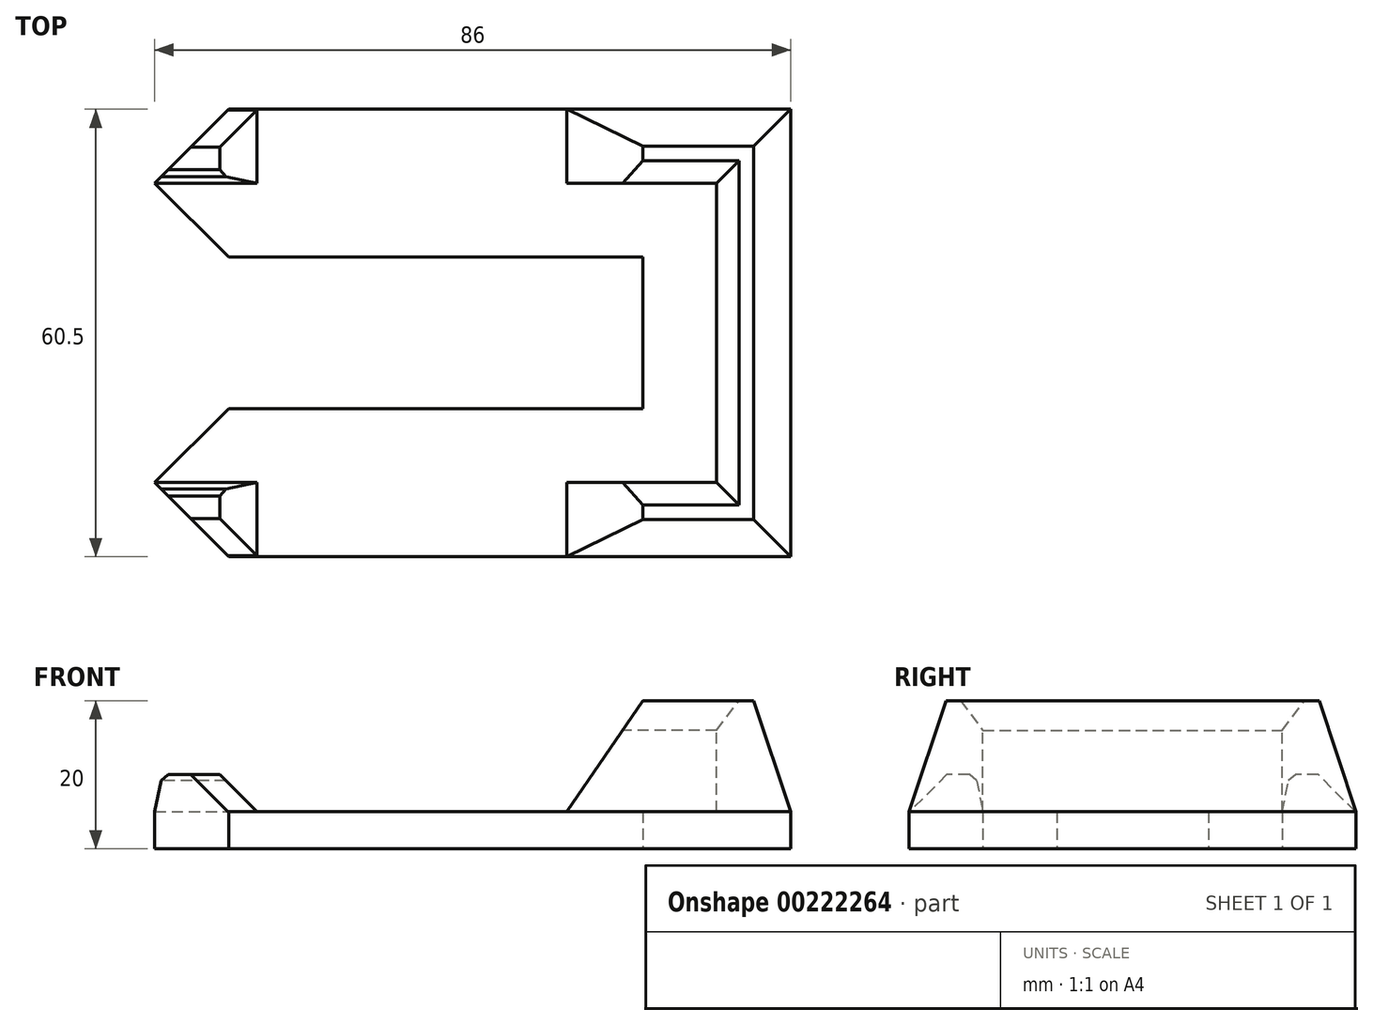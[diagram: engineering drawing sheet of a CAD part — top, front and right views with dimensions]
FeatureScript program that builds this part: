
annotation { "Feature Type Name" : "Feature", "Feature Type Description" : "" }
export const myFeature = defineFeature(function(context is Context, id is Id, definition is map)
    precondition{}
    {
        {
            var Q0;
            Q0=qCreatedBy(makeId("Top.planeOp"),FACE);
            var sketch = newSketch(context, id + "F0", { "sketchPlane" : qUnion([Q0])});
            skLineSegment(sketch, "E0.bottom", {"start": v(76, -20.25) * mm, "end": v(-76, -20.25) * mm, "construction": true});
            skLineSegment(sketch, "E0.top", {"start": v(76, 20.25) * mm, "end": v(-76, 20.25) * mm, "construction": true});
            skLineSegment(sketch, "E0.left", {"start": v(76, -20.25) * mm, "end": v(76, 20.25) * mm, "construction": true});
            skLineSegment(sketch, "E0.right", {"start": v(-76, -20.25) * mm, "end": v(-76, 20.25) * mm, "construction": true});
            skPoint(sketch, "E0.middle", {"position": v(0, 0) * mm});
            skLineSegment(sketch, "E1.bottom", {"start": v(86, -30.25) * mm, "end": v(-86, -30.25) * mm});
            skLineSegment(sketch, "E1.top", {"start": v(86, 30.25) * mm, "end": v(-86, 30.25) * mm});
            skLineSegment(sketch, "E1.left", {"start": v(86, -30.25) * mm, "end": v(86, 30.25) * mm});
            skLineSegment(sketch, "E1.right", {"start": v(-86, -30.25) * mm, "end": v(-86, 30.25) * mm});
            skSolve(sketch);
        }
        {
            var Q0;
            Q0=qCreatedBy(makeId("Top.planeOp"),FACE);
            cPlane(context, id + "F1", {"entities" : qUnion([Q0]), "cplaneType" : CPlaneType.OFFSET, "offset" : 15 * mm, "width" : 150 * mm, "height" : 150 * mm});
        }
        {
            var Q0;
            Q0=qCreatedBy(id+"F1.planeOp",FACE);
            var sketch = newSketch(context, id + "F2", { "sketchPlane" : qUnion([Q0])});
            skPoint(sketch, "E2.0", {"position": v(-86, -30.25) * mm});
            skPoint(sketch, "E3.0", {"position": v(-76, -20.25) * mm});
            skLineSegment(sketch, "E4", {"start": v(-76, 0) * mm, "end": v(-76, -20.25) * mm});
            skLineSegment(sketch, "E5", {"start": v(-76, -20.25) * mm, "end": v(-86, -30.25) * mm, "construction": true});
            skPoint(sketch, "E6", {"position": v(-81, -25.25) * mm});
            skLineSegment(sketch, "E7", {"start": v(-76, 0) * mm, "end": v(-81, 0) * mm});
            skLineSegment(sketch, "E8", {"start": v(-81, 0) * mm, "end": v(-81, -25.25) * mm});
            skLineSegment(sketch, "E9", {"start": v(-76, -20.25) * mm, "end": v(-66, -20.25) * mm});
            skLineSegment(sketch, "E10", {"start": v(-66, -20.25) * mm, "end": v(-66, -25.25) * mm});
            skLineSegment(sketch, "E11", {"start": v(-66, -25.25) * mm, "end": v(-81, -25.25) * mm});
            skSolve(sketch);
        }
        {
            var Q0;
            Q0=qCreatedBy(makeId("Top.planeOp"),FACE);
            var sketch = newSketch(context, id + "F3", { "sketchPlane" : qUnion([Q0])});
            skPoint(sketch, "E12.0", {"position": v(-86, -30.25) * mm});
            skPoint(sketch, "E13.0", {"position": v(-76, -20.25) * mm});
            skLineSegment(sketch, "E14", {"start": v(-86, -30.25) * mm, "end": v(-86, 0) * mm});
            skLineSegment(sketch, "E15", {"start": v(-86, 0) * mm, "end": v(-76, 0) * mm});
            skLineSegment(sketch, "E16", {"start": v(-76, 0) * mm, "end": v(-76, -20.25) * mm});
            skLineSegment(sketch, "E17", {"start": v(-76, -20.25) * mm, "end": v(-86, -30.25) * mm, "construction": true});
            skLineSegment(sketch, "E18.MirrorCS", {"start": v(-55.75, -20.25) * mm, "end": v(-76, -20.25) * mm});
            skLineSegment(sketch, "E19.MirrorCS", {"start": v(-86, -30.25) * mm, "end": v(-55.75, -30.25) * mm});
            skLineSegment(sketch, "E20.MirrorCS", {"start": v(-55.75, -30.25) * mm, "end": v(-55.75, -20.25) * mm});
            skLineSegment(sketch, "E21", {"start": v(0, 0) * mm, "end": v(-88.2, 0) * mm, "construction": true});
            skSolve(sketch);
        }
        {
            var Q0;
            Q0=makeQuery(id+"F0.imprint","IMPRINT",FACE,{"disambiguationData":[TD([[makeQuery(id+"F0.imprint","IMPRINT",EDGE,{"derivedFrom":sQuery(id+"F0.wireOp",EDGE,"E1.bottom")}),-1.0]])]});
            extrude(context, id + "F4", {"entities" : qUnion([Q0]), "oppositeDirection" : true, "depth" : 5 * mm});
        }
        {
            var Q1;
            Q1=makeQuery(id+"F3.imprint","IMPRINT",FACE,{"disambiguationData":[TD([[makeQuery(id+"F3.imprint","IMPRINT",EDGE,{"derivedFrom":sQuery(id+"F3.wireOp",EDGE,"E14")}),-1.0]])]});
            var Q2;
            Q2=makeQuery(id+"F2.imprint","IMPRINT",FACE,{"disambiguationData":[TD([[makeQuery(id+"F2.imprint","IMPRINT",EDGE,{"derivedFrom":sQuery(id+"F2.wireOp",EDGE,"E4")}),-1.0]])]});
            loft(context, id + "F5", {"operationType" : NewBodyOperationType.ADD, "sheetProfilesArray" : [{ "sheetProfileEntities" : qUnion([Q1]) }, { "sheetProfileEntities" : qUnion([Q2]) }]});
        }
        {
            var Q0;
            Q0=makeQuery(id+"F5.opLoft","MID_CAP_EDGE",EDGE,{"disambiguationData":[OSD([sQuery(id+"F2.wireOp",EDGE,"E4"),sQuery(id+"F2.wireOp",EDGE,"E7"),sQuery(id+"F2.wireOp",EDGE,"E9")])],"capPos":1.0});
            var Q1;
            Q1=makeQuery(id+"F5.opLoft","MID_CAP_EDGE",EDGE,{"disambiguationData":[OSD([sQuery(id+"F2.wireOp",EDGE,"E4"),sQuery(id+"F2.wireOp",EDGE,"E9"),sQuery(id+"F2.wireOp",EDGE,"E10")])],"capPos":1.0});
            chamfer(context, id + "F6", {"entities" : qUnion([Q0, Q1]), "chamferType" : ChamferType.TWO_OFFSETS, "width1" : 3 * mm, "oppositeDirection" : false, "width2" : 4 * mm, "tangentPropagation" : true});
        }
        {
            var Q0;
            Q0=makeQuery(id+"F4.opExtrude","SWEPT_BODY",BODY,{"disambiguationData":[OSD([sQuery(id+"F0.wireOp",EDGE,"E1.bottom"),sQuery(id+"F0.wireOp",EDGE,"E1.top"),sQuery(id+"F0.wireOp",EDGE,"E1.left"),sQuery(id+"F0.wireOp",EDGE,"E1.right")])]});
            var Q1;
            Q1=qCreatedBy(makeId("Right.planeOp"),FACE);
            mirror(context, id + "F7", {"operationType" : NewBodyOperationType.ADD, "entities" : qUnion([Q0]), "mirrorPlane" : qUnion([Q1])});
        }
        {
            var Q0;
            Q0=makeQuery(id+"F0.imprint","IMPRINT",FACE,{"disambiguationData":[TD([[makeQuery(id+"F0.imprint","IMPRINT",EDGE,{"derivedFrom":sQuery(id+"F0.wireOp",EDGE,"E1.bottom")}),-1.0]])]});
            var sketch = newSketch(context, id + "F8", { "sketchPlane" : qUnion([Q0])});
            skLineSegment(sketch, "E22", {"start": v(0, 45.4) * mm, "end": v(0, -36.03) * mm, "construction": true});
            skLineSegment(sketch, "E23", {"start": v(0, -20.25) * mm, "end": v(13.82, -20.25) * mm});
            skLineSegment(sketch, "E24", {"start": v(13.82, -20.25) * mm, "end": v(13.82, -30.13) * mm});
            skLineSegment(sketch, "E25", {"start": v(13.82, -30.13) * mm, "end": v(0, -30.13) * mm});
            skLineSegment(sketch, "E26.MirrorCS", {"start": v(-13.82, -30.13) * mm, "end": v(0, -30.13) * mm});
            skLineSegment(sketch, "E27.MirrorCS", {"start": v(0, -20.25) * mm, "end": v(-13.82, -20.25) * mm});
            skLineSegment(sketch, "E28.MirrorCS", {"start": v(-13.82, -20.25) * mm, "end": v(-13.82, -30.13) * mm});
            skSolve(sketch);
        }
        {
            var Q0;
            Q0=qSketchRegion(id+"F8",true);
            extrude(context, id + "F9", {"entities" : qUnion([Q0]), "operationType" : NewBodyOperationType.ADD, "depth" : 5 * mm});
        }
        {
            var Q0;
            Q0=makeQuery(id+"F9.opExtrude","CAP_EDGE",EDGE,{"disambiguationData":[OSD([sQuery(id+"F8.wireOp",EDGE,"E24")])],"isStart":false});
            var Q1;
            Q1=makeQuery(id+"F9.opExtrude","CAP_EDGE",EDGE,{"disambiguationData":[OSD([sQuery(id+"F8.wireOp",EDGE,"E25"),sQuery(id+"F8.wireOp",EDGE,"E26.MirrorCS")])],"isStart":false});
            var Q2;
            Q2=makeQuery(id+"F9.opExtrude","CAP_EDGE",EDGE,{"disambiguationData":[OSD([sQuery(id+"F8.wireOp",EDGE,"E28.MirrorCS")])],"isStart":false});
            chamfer(context, id + "F10", {"entities" : qUnion([Q0, Q1, Q2]), "width" : 5 * mm, "tangentPropagation" : true});
        }
        {
            var Q0;
            Q0=makeQuery(id+"F9.opExtrude","CAP_EDGE",EDGE,{"disambiguationData":[OSD([sQuery(id+"F8.wireOp",EDGE,"E23"),sQuery(id+"F8.wireOp",EDGE,"E27.MirrorCS")])],"isStart":false});
            chamfer(context, id + "F11", {"entities" : qUnion([Q0]), "chamferType" : ChamferType.TWO_OFFSETS, "width1" : 5 * mm, "oppositeDirection" : false, "width2" : 1 * mm, "tangentPropagation" : true});
        }
        {
            var Q0;
            {var subQ0=sQuery(id+"F8.wireOp",EDGE,"E27.MirrorCS");var subQ1=sQuery(id+"F8.wireOp",EDGE,"E23");Q0=makeQuery(id+"F11.opChamfer","BLEND_EDGE",EDGE,{"blendedFrom":[makeQuery(id+"F9.opExtrude","CAP_EDGE",EDGE,{"disambiguationData":[OSD([subQ1,subQ0])],"isStart":false}),makeQuery(id+"F9.opExtrude","CAP_FACE",FACE,{"disambiguationData":[OSD([subQ1,sQuery(id+"F8.wireOp",EDGE,"E24"),sQuery(id+"F8.wireOp",EDGE,"E25"),subQ0,sQuery(id+"F8.wireOp",EDGE,"E28.MirrorCS"),sQuery(id+"F8.wireOp",EDGE,"E26.MirrorCS")])],"isStart":false})],"blendedInto":[makeQuery(id+"F9.opExtrude","CAP_FACE",FACE,{"disambiguationData":[OSD([subQ1,sQuery(id+"F8.wireOp",EDGE,"E24"),sQuery(id+"F8.wireOp",EDGE,"E25"),subQ0,sQuery(id+"F8.wireOp",EDGE,"E28.MirrorCS"),sQuery(id+"F8.wireOp",EDGE,"E26.MirrorCS")])],"isStart":false})]});}
            chamfer(context, id + "F12", {"entities" : qUnion([Q0]), "width" : 1 * mm, "tangentPropagation" : true});
        }
        {
            var Q0;
            Q0=makeQuery(id+"F4.opExtrude","SWEPT_BODY",BODY,{"disambiguationData":[OSD([sQuery(id+"F0.wireOp",EDGE,"E1.bottom"),sQuery(id+"F0.wireOp",EDGE,"E1.top"),sQuery(id+"F0.wireOp",EDGE,"E1.left"),sQuery(id+"F0.wireOp",EDGE,"E1.right")])]});
            var Q1;
            Q1=qCreatedBy(makeId("Front.planeOp"),FACE);
            mirror(context, id + "F13", {"operationType" : NewBodyOperationType.ADD, "entities" : qUnion([Q0]), "mirrorPlane" : qUnion([Q1])});
        }
        {
            var Q0;
            Q0=qCreatedBy(makeId("Top.planeOp"),FACE);
            var sketch = newSketch(context, id + "F14", { "sketchPlane" : qUnion([Q0])});
            skLineSegment(sketch, "E29.bottom", {"start": v(66, -10.25) * mm, "end": v(-66, -10.25) * mm});
            skLineSegment(sketch, "E29.top", {"start": v(66, 10.25) * mm, "end": v(-66, 10.25) * mm});
            skLineSegment(sketch, "E29.left", {"start": v(66, -10.25) * mm, "end": v(66, 10.25) * mm});
            skLineSegment(sketch, "E29.right", {"start": v(-66, -10.25) * mm, "end": v(-66, 10.25) * mm});
            skPoint(sketch, "E29.middle", {"position": v(0, 0) * mm});
            skLineSegment(sketch, "E30.0", {"start": v(-76, -20.25) * mm, "end": v(-76, 20.25) * mm, "construction": true});
            skLineSegment(sketch, "E31.0", {"start": v(76, 20.25) * mm, "end": v(-76, 20.25) * mm, "construction": true});
            skSolve(sketch);
        }
        {
            var Q0;
            Q0=qSketchRegion(id+"F14",true);
            extrude(context, id + "F15", {"entities" : qUnion([Q0]), "operationType" : NewBodyOperationType.REMOVE, "endBound" : BoundingType.SYMMETRIC, "depth" : 25 * mm});
        }
        {
            var Q0;
            Q0=qCreatedBy(makeId("Top.planeOp"),FACE);
            var sketch = newSketch(context, id + "F16", { "sketchPlane" : qUnion([Q0])});
            skLineSegment(sketch, "E32.0", {"start": v(76, 20.25) * mm, "end": v(-76, 20.25) * mm, "construction": true});
            skLineSegment(sketch, "E32.1", {"start": v(-66, 10.25) * mm, "end": v(66, 10.25) * mm, "construction": true});
            skLineSegment(sketch, "E32.2", {"start": v(86, 30.25) * mm, "end": v(-86, 30.25) * mm, "construction": true});
            skPoint(sketch, "E32.3", {"position": v(0, 20.25) * mm});
            skLineSegment(sketch, "E33", {"start": v(0, 20.25) * mm, "end": v(18.64, 1.6) * mm});
            skLineSegment(sketch, "E34", {"start": v(18.64, 1.6) * mm, "end": v(18.64, -1.6) * mm});
            skLineSegment(sketch, "E35", {"start": v(18.64, -1.6) * mm, "end": v(0, -20.25) * mm});
            skLineSegment(sketch, "E36", {"start": v(0, -20.25) * mm, "end": v(26.9, -47.14) * mm});
            skLineSegment(sketch, "E37", {"start": v(26.9, -47.14) * mm, "end": v(91.07, -47.14) * mm});
            skLineSegment(sketch, "E38", {"start": v(91.07, -47.14) * mm, "end": v(91.07, 44.05) * mm});
            skLineSegment(sketch, "E39", {"start": v(91.07, 44.05) * mm, "end": v(23.8, 44.05) * mm});
            skLineSegment(sketch, "E40", {"start": v(23.8, 44.05) * mm, "end": v(0, 20.25) * mm});
            skSolve(sketch);
        }
        {
            var Q0;
            {var subQ5=sQuery(id+"F16.wireOp",EDGE,"E33");Q0=makeQuery(id+"F16.imprint","IMPRINT",FACE,{"disambiguationData":[TD([[makeQuery(id+"F16.imprint","IMPRINT",EDGE,{"derivedFrom":subQ5}),1.0]])]});}
            var Q1;
            {var subQ1=sQuery(id+"F16.wireOp",EDGE,"E37");Q1=makeQuery(id+"F16.imprint","IMPRINT",FACE,{"disambiguationData":[TD([[makeQuery(id+"F16.imprint","IMPRINT",EDGE,{"derivedFrom":subQ1}),1.0]])]});}
            extrude(context, id + "F17", {"entities" : qUnion([Q0, Q1]), "depth" : 25 * mm, "hasSecondDirection" : true, "secondDirectionOppositeDirection" : true, "secondDirectionDepth" : 25 * mm});
        }
        {
            var Q0;
            Q0=makeQuery(id+"F17.opExtrude","SWEPT_BODY",BODY,{"disambiguationData":[OSD([sQuery(id+"F16.wireOp",EDGE,"E33"),sQuery(id+"F16.wireOp",EDGE,"E34"),sQuery(id+"F16.wireOp",EDGE,"E35"),sQuery(id+"F16.wireOp",EDGE,"E36"),sQuery(id+"F16.wireOp",EDGE,"E37"),sQuery(id+"F16.wireOp",EDGE,"E38"),sQuery(id+"F16.wireOp",EDGE,"E39"),sQuery(id+"F16.wireOp",EDGE,"E40")])]});
            var Q1;
            Q1=makeQuery(id+"F4.opExtrude","SWEPT_BODY",BODY,{"disambiguationData":[OSD([sQuery(id+"F0.wireOp",EDGE,"E1.bottom"),sQuery(id+"F0.wireOp",EDGE,"E1.top"),sQuery(id+"F0.wireOp",EDGE,"E1.left"),sQuery(id+"F0.wireOp",EDGE,"E1.right")])]});
            var Q2;
            Q2=makeQuery(id+"F4.opExtrude","SWEPT_BODY",BODY,{"disambiguationData":[OSD([sQuery(id+"F0.wireOp",EDGE,"E1.bottom"),sQuery(id+"F0.wireOp",EDGE,"E1.top"),sQuery(id+"F0.wireOp",EDGE,"E1.left"),sQuery(id+"F0.wireOp",EDGE,"E1.right")])]});
            booleanBodies(context, id + "F18", {"operationType" : BooleanOperationType.INTERSECTION, "tools" : qUnion([Q0, Q1]), "targets" : qUnion([Q2])});
        }
    });
